# Revit family: Robe_Hook-Double-American_Standard-Traditional-8334210.002
name_source: partatom
category: Specialty Equipment
units: mm (PartAtom-declared; Revit-internal decimal feet)

## family parameters
Cut with Voids When Loaded = No
Host = Face
OmniClass Number = 23.40.20.21.31
OmniClass Title = Robe Hooks
Part Type = Normal
Room Calculation Point = No
Round Connector Dimension = Use Diameter
Shared = Yes

## types (1)
- 8334210.002
    Assembly Code = C1030220
    Default Elevation = 40"
    Description = Traditional TR Series Double Robe Hook
    Finish = Metal-American Standard-002-Polished Chrome
    Height = 3 1/4"
    Installation Instruction Link = https://lixil.cdn.celum.cloud
    Installation Type = Wall Mounted
    Length = 3 3/4"
    Manufacturer = American Standard
    Material = Metal-American Standard-002-Polished Chrome
    Model = 8334210.002
    Product Documentation Link = https://lixil.cdn.celum.cloud
    Product Page URL = https://www.americanstandard.ca
    Revised Date = 11/03/2024
    URL = https://www.americanstandard.ca
    Warranty Information = 1 Year Warranty
    Width = 4 1/8"

## geometry (parser evidence)
native form markers: Sweep x2
no freeform markers — native parametric forms only
